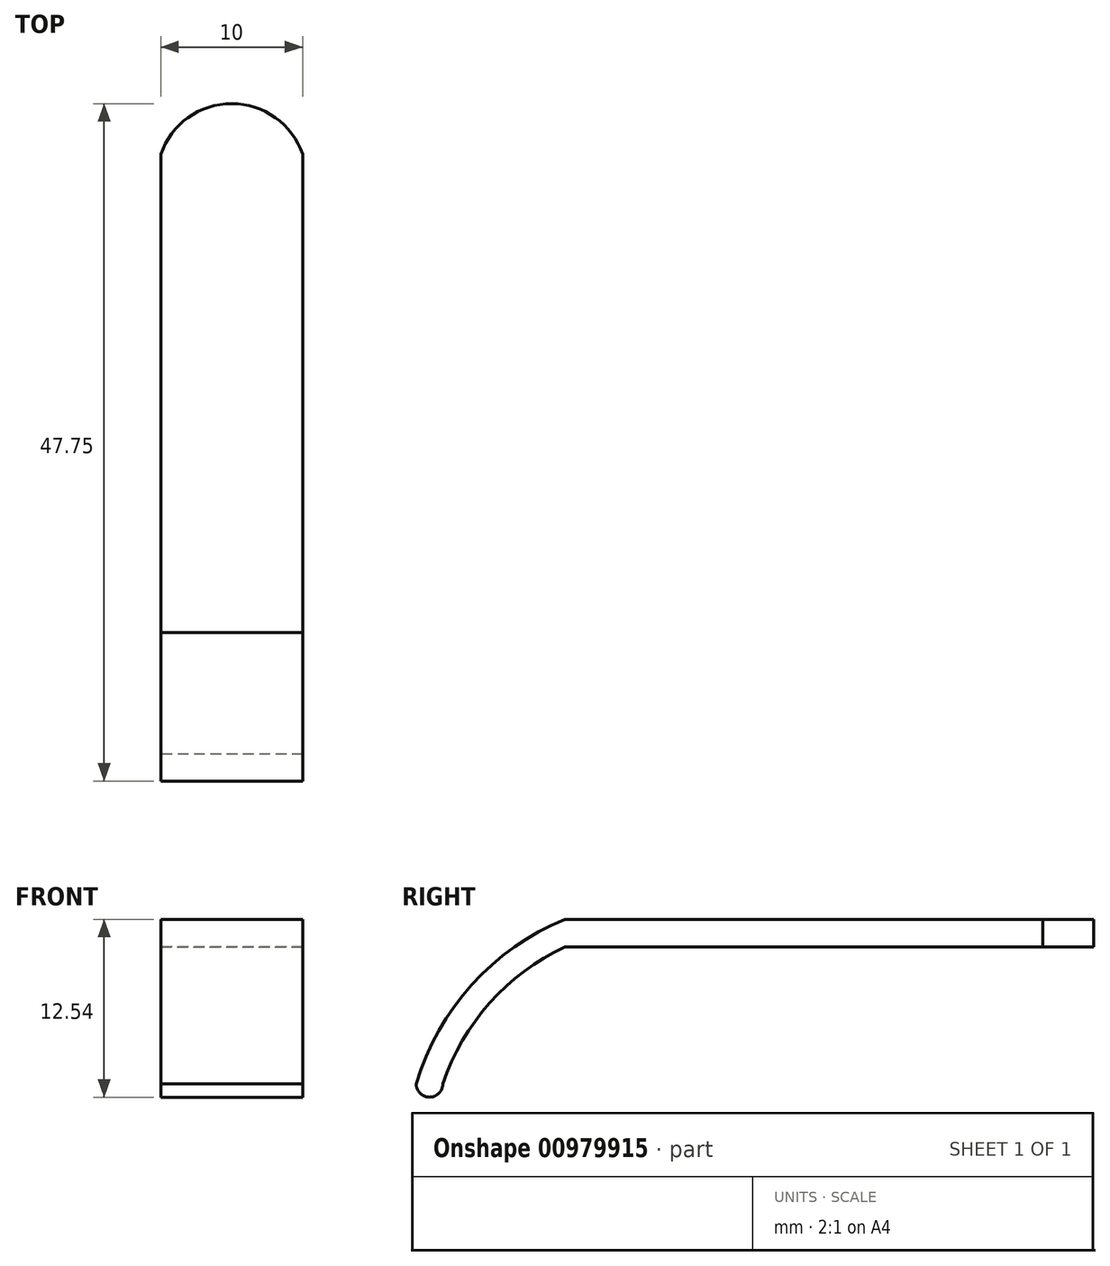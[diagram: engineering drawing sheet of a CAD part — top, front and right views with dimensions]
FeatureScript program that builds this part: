
annotation { "Feature Type Name" : "Feature", "Feature Type Description" : "" }
export const myFeature = defineFeature(function(context is Context, id is Id, definition is map)
    precondition{}
    {
        {
            var Q0;
            Q0=qCreatedBy(makeId("Right.planeOp"),FACE);
            var sketch = newSketch(context, id + "F0", { "sketchPlane" : qUnion([Q0])});
            skArc(sketch, "E0", {"start": v(10.47, 11.59) * mm, "mid": v(3.93, 6.98) * mm, "end": v(0, 0) * mm});
            skLineSegment(sketch, "E1", {"start": v(10.47, 11.59) * mm, "end": v(48.45, 11.59) * mm});
            skLineSegment(sketch, "E2", {"start": v(48.45, 9.63) * mm, "end": v(10.47, 9.63) * mm});
            skArc(sketch, "E3", {"start": v(10.47, 9.63) * mm, "mid": v(5.19, 5.7) * mm, "end": v(1.88, 0) * mm});
            skArc(sketch, "E4", {"start": v(0, 0) * mm, "mid": v(0.94, -0.95) * mm, "end": v(1.88, 0) * mm});
            skLineSegment(sketch, "E5", {"start": v(48.45, 11.59) * mm, "end": v(48.45, 9.63) * mm});
            skSolve(sketch);
        }
        {
            var Q0;
            Q0 = qSketchRegion(id + "F0", true);
            extrude(context, id + "F1", {"entities" : qUnion([Q0]), "depth" : 10 * mm, "offsetDistance" : 25 * mm});
        }
        {
            var Q0;
            Q0=makeQuery(id+"F1.opExtrude","SWEPT_FACE",FACE,{"disambiguationData":[OSD([sQuery(id+"F0.wireOp",EDGE,"E1")])]});
            var sketch = newSketch(context, id + "F2", { "sketchPlane" : qUnion([Q0])});
            skLineSegment(sketch, "E6", {"start": v(5, 48.45) * mm, "end": v(5, 36.48) * mm, "construction": true});
            skArc(sketch, "E7", {"start": v(10, 44.17) * mm, "mid": v(5, 47.75) * mm, "end": v(0, 44.17) * mm});
            skSolve(sketch);
        }
        {
            var Q0;
            {var subQ0=sQuery(id+"F2.wireOp",EDGE,"E7");Q0=makeQuery(id+"F2.imprint","IMPRINT",FACE,{"disambiguationData":[TD([[makeQuery(id+"F2.imprint","IMPRINT",EDGE,{"derivedFrom":subQ0}),-1.0]])]});}
            extrude(context, id + "F3", {"entities" : qUnion([Q0]), "operationType" : NewBodyOperationType.REMOVE, "oppositeDirection" : true, "depth" : 25 * mm, "offsetDistance" : 25 * mm});
        }
    });
